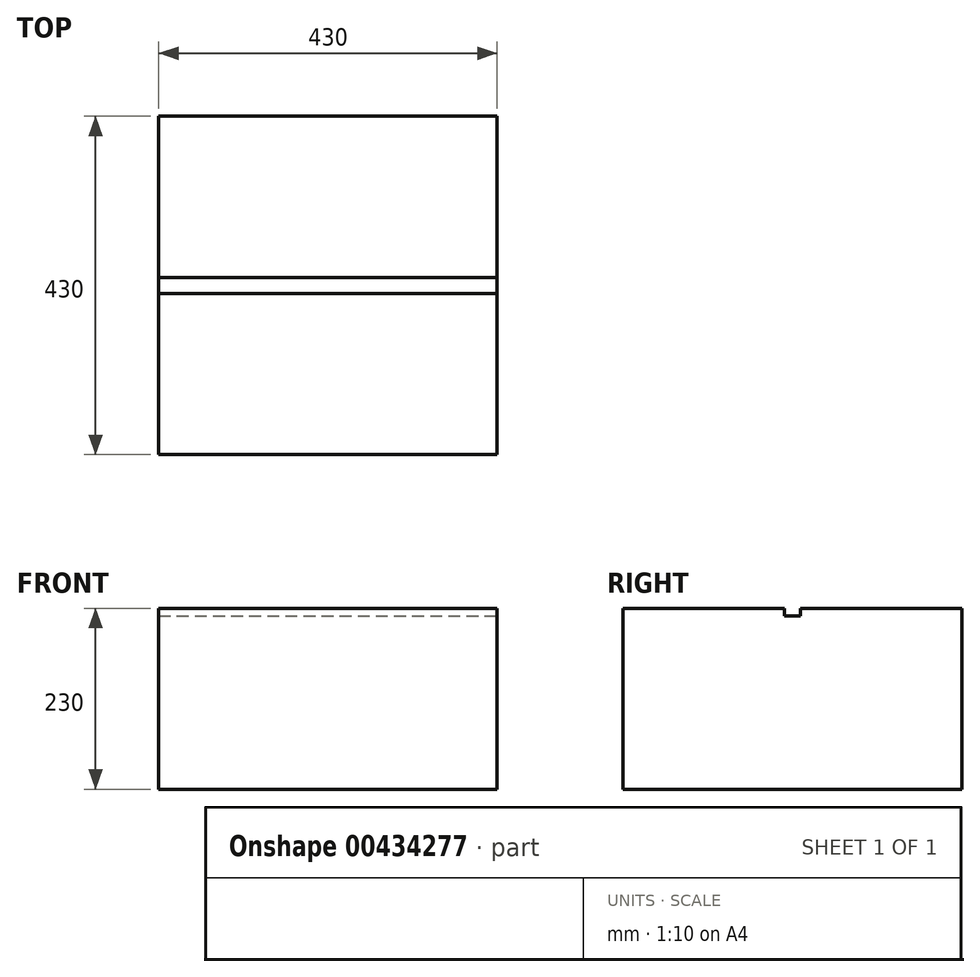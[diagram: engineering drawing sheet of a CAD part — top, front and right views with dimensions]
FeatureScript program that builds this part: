
annotation { "Feature Type Name" : "Feature", "Feature Type Description" : "" }
export const myFeature = defineFeature(function(context is Context, id is Id, definition is map)
    precondition{}
    {
        {
            var Q0;
            Q0=qCreatedBy(makeId("Right.planeOp"),FACE);
            var sketch = newSketch(context, id + "F0", { "sketchPlane" : qUnion([Q0])});
            skLineSegment(sketch, "E0.bottom", {"start": v(-160.6, 93.56) * mm, "end": v(269.4, 93.56) * mm});
            skLineSegment(sketch, "E0.top", {"start": v(-160.6, -136.44) * mm, "end": v(269.4, -136.44) * mm});
            skLineSegment(sketch, "E0.left", {"start": v(-160.6, 93.56) * mm, "end": v(-160.6, -136.44) * mm});
            skLineSegment(sketch, "E0.right", {"start": v(269.4, 93.56) * mm, "end": v(269.4, -136.44) * mm});
            skSolve(sketch);
        }
        {
            var Q0;
            Q0=qSketchRegion(id+"F0",true);
            extrude(context, id + "F1", {"entities" : qUnion([Q0]), "oppositeDirection" : true, "depth" : 430 * mm});
        }
        {
            var Q0;
            Q0=makeQuery(id+"F1.opExtrude","CAP_FACE",FACE,{"disambiguationData":[OSD([sQuery(id+"F0.wireOp",EDGE,"E0.bottom"),sQuery(id+"F0.wireOp",EDGE,"E0.top"),sQuery(id+"F0.wireOp",EDGE,"E0.left"),sQuery(id+"F0.wireOp",EDGE,"E0.right")])],"isStart":true});
            var sketch = newSketch(context, id + "F2", { "sketchPlane" : qUnion([Q0])});
            skLineSegment(sketch, "E1.bottom", {"start": v(44.4, 93.56) * mm, "end": v(64.4, 93.56) * mm});
            skLineSegment(sketch, "E1.top", {"start": v(44.4, 83.56) * mm, "end": v(64.4, 83.56) * mm});
            skLineSegment(sketch, "E1.left", {"start": v(44.4, 93.56) * mm, "end": v(44.4, 83.56) * mm});
            skLineSegment(sketch, "E1.right", {"start": v(64.4, 93.56) * mm, "end": v(64.4, 83.56) * mm});
            skLineSegment(sketch, "E2.top", {"start": v(54.4, 93.56) * mm, "end": v(93.02, 93.56) * mm});
            skLineSegment(sketch, "E2.left", {"start": v(54.4, 93.56) * mm, "end": v(54.4, 93.56) * mm});
            skLineSegment(sketch, "E2.right", {"start": v(93.02, 82.94) * mm, "end": v(93.02, 93.56) * mm});
            skSolve(sketch);
        }
        {
            var Q0;
            Q0=qSketchRegion(id+"F2",true);
            extrude(context, id + "F3", {"entities" : qUnion([Q0]), "operationType" : NewBodyOperationType.REMOVE, "oppositeDirection" : true, "depth" : 560 * mm});
        }
    });
